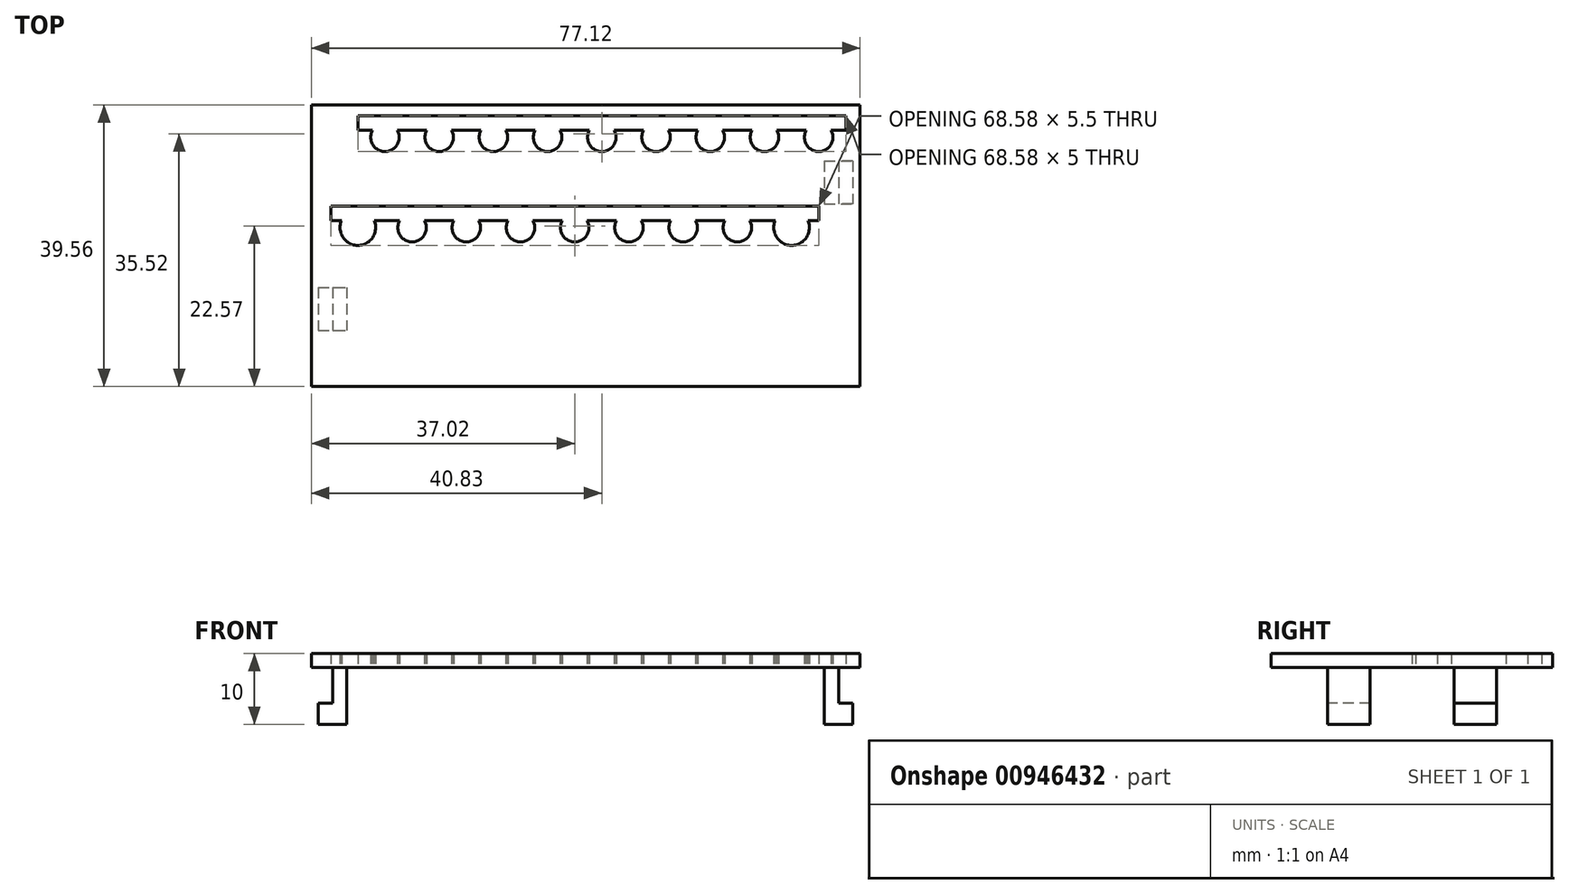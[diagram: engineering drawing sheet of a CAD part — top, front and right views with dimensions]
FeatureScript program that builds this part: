
annotation { "Feature Type Name" : "Feature", "Feature Type Description" : "" }
export const myFeature = defineFeature(function(context is Context, id is Id, definition is map)
    precondition{}
    {
        {
            var Q0;
            Q0=qCreatedBy(makeId("Top.planeOp"),FACE);
            var sketch = newSketch(context, id + "F0", { "sketchPlane" : qUnion([Q0])});
            skLineSegment(sketch, "E0.bottom", {"start": v(0, 39.56) * mm, "end": v(77.12, 39.56) * mm});
            skLineSegment(sketch, "E0.top", {"start": v(0, 0) * mm, "end": v(77.12, 0) * mm});
            skLineSegment(sketch, "E0.left", {"start": v(0, 39.56) * mm, "end": v(0, 0) * mm});
            skLineSegment(sketch, "E0.right", {"start": v(77.12, 39.56) * mm, "end": v(77.12, 0) * mm});
            skCircle(sketch, "E1", {"center": v(10.35, 35.02) * mm, "radius": 2 * mm});
            skCircle(sketch, "E2", {"center": v(14.16, 22.32) * mm, "radius": 2 * mm});
            skCircle(sketch, "E3.1.0.0", {"center": v(17.97, 35.02) * mm, "radius": 2 * mm});
            skCircle(sketch, "E3.2.0.0", {"center": v(25.6, 35.02) * mm, "radius": 2 * mm});
            skCircle(sketch, "E3.3.0.0", {"center": v(33.2, 35.02) * mm, "radius": 2 * mm});
            skCircle(sketch, "E3.4.0.0", {"center": v(40.83, 35.02) * mm, "radius": 2 * mm});
            skCircle(sketch, "E3.5.0.0", {"center": v(48.45, 35.02) * mm, "radius": 2 * mm});
            skCircle(sketch, "E3.6.0.0", {"center": v(56.07, 35.02) * mm, "radius": 2 * mm});
            skCircle(sketch, "E3.7.0.0", {"center": v(63.7, 35.02) * mm, "radius": 2 * mm});
            skCircle(sketch, "E3.8.0.0", {"center": v(71.31, 35.02) * mm, "radius": 2 * mm});
            skLineSegment(sketch, "E3.direction1", {"start": v(10.35, 35.02) * mm, "end": v(17.97, 35.02) * mm, "construction": true});
            skCircle(sketch, "E4.1.0.0", {"center": v(21.78, 22.32) * mm, "radius": 2 * mm});
            skCircle(sketch, "E4.2.0.0", {"center": v(29.4, 22.32) * mm, "radius": 2 * mm});
            skCircle(sketch, "E4.3.0.0", {"center": v(37.02, 22.32) * mm, "radius": 2 * mm});
            skCircle(sketch, "E4.4.0.0", {"center": v(44.64, 22.32) * mm, "radius": 2 * mm});
            skCircle(sketch, "E4.5.0.0", {"center": v(52.26, 22.32) * mm, "radius": 2 * mm});
            skCircle(sketch, "E4.6.0.0", {"center": v(59.88, 22.32) * mm, "radius": 2 * mm});
            skLineSegment(sketch, "E4.direction1", {"start": v(14.16, 22.32) * mm, "end": v(21.78, 22.32) * mm, "construction": true});
            skCircle(sketch, "E5", {"center": v(6.54, 22.32) * mm, "radius": 2.5 * mm});
            skCircle(sketch, "E6.1.0.0", {"center": v(67.5, 22.32) * mm, "radius": 2.5 * mm});
            skLineSegment(sketch, "E6.direction1", {"start": v(6.54, 22.32) * mm, "end": v(67.5, 22.32) * mm, "construction": true});
            skLineSegment(sketch, "E7.bottom", {"start": v(72.12, 31.67) * mm, "end": v(74.12, 31.67) * mm});
            skLineSegment(sketch, "E7.top", {"start": v(72.12, 25.67) * mm, "end": v(74.12, 25.67) * mm});
            skLineSegment(sketch, "E7.left", {"start": v(72.12, 31.67) * mm, "end": v(72.12, 25.67) * mm});
            skLineSegment(sketch, "E7.right", {"start": v(74.12, 31.67) * mm, "end": v(74.12, 25.67) * mm});
            skLineSegment(sketch, "E8.bottom", {"start": v(3, 13.89) * mm, "end": v(5, 13.89) * mm});
            skLineSegment(sketch, "E8.top", {"start": v(3, 7.89) * mm, "end": v(5, 7.89) * mm});
            skLineSegment(sketch, "E8.left", {"start": v(3, 13.89) * mm, "end": v(3, 7.89) * mm});
            skLineSegment(sketch, "E8.right", {"start": v(5, 13.89) * mm, "end": v(5, 7.89) * mm});
            skLineSegment(sketch, "E9.bottom", {"start": v(2.73, 25.32) * mm, "end": v(71.31, 25.32) * mm});
            skLineSegment(sketch, "E9.top", {"start": v(2.73, 23.32) * mm, "end": v(71.31, 23.32) * mm});
            skLineSegment(sketch, "E9.left", {"start": v(2.73, 25.32) * mm, "end": v(2.73, 23.32) * mm});
            skLineSegment(sketch, "E9.right", {"start": v(71.31, 25.32) * mm, "end": v(71.31, 23.32) * mm});
            skLineSegment(sketch, "E10.bottom", {"start": v(6.54, 38.02) * mm, "end": v(75.12, 38.02) * mm});
            skLineSegment(sketch, "E10.top", {"start": v(6.54, 36.02) * mm, "end": v(75.12, 36.02) * mm});
            skLineSegment(sketch, "E10.left", {"start": v(6.54, 38.02) * mm, "end": v(6.54, 36.02) * mm});
            skLineSegment(sketch, "E10.right", {"start": v(75.12, 38.02) * mm, "end": v(75.12, 36.02) * mm});
            skSolve(sketch);
        }
        {
            var Q0;
            Q0=makeQuery(id+"F0.imprint","IMPRINT",FACE,{"disambiguationData":[TD([[makeQuery(id+"F0.imprint","IMPRINT",EDGE,{"derivedFrom":sQuery(id+"F0.wireOp",EDGE,"E0.bottom")}),-1.0]])]});
            extrude(context, id + "F1", {"entities" : qUnion([Q0]), "depth" : 2 * mm, "offsetDistance" : 25 * mm});
        }
        {
            var Q0;
            Q0=makeQuery(id+"F0.imprint","IMPRINT",FACE,{"disambiguationData":[TD([[makeQuery(id+"F0.imprint","IMPRINT",EDGE,{"derivedFrom":sQuery(id+"F0.wireOp",EDGE,"E7.bottom")}),-1.0]])]});
            extrude(context, id + "F2", {"entities" : qUnion([Q0]), "operationType" : NewBodyOperationType.ADD, "depth" : -8 * mm, "offsetDistance" : 25 * mm, "hasSecondDirection" : true, "secondDirectionOppositeDirection" : true, "secondDirectionDepth" : -2 * mm});
        }
        {
            var Q0;
            Q0=makeQuery(id+"F0.imprint","IMPRINT",FACE,{"disambiguationData":[TD([[makeQuery(id+"F0.imprint","IMPRINT",EDGE,{"derivedFrom":sQuery(id+"F0.wireOp",EDGE,"E8.bottom")}),-1.0]])]});
            extrude(context, id + "F3", {"entities" : qUnion([Q0]), "operationType" : NewBodyOperationType.ADD, "depth" : -8 * mm, "offsetDistance" : 25 * mm, "hasSecondDirection" : true, "secondDirectionOppositeDirection" : true, "secondDirectionDepth" : -2 * mm});
        }
        {
            var Q0;
            Q0=makeQuery(id+"F3.opExtrude","SWEPT_FACE",FACE,{"disambiguationData":[OSD([sQuery(id+"F0.wireOp",EDGE,"E8.right")])]});
            var sketch = newSketch(context, id + "F4", { "sketchPlane" : qUnion([Q0])});
            skLineSegment(sketch, "E11.bottom", {"start": v(7.89, -5) * mm, "end": v(13.89, -5) * mm});
            skLineSegment(sketch, "E11.top", {"start": v(7.89, -8) * mm, "end": v(13.89, -8) * mm});
            skLineSegment(sketch, "E11.left", {"start": v(7.89, -5) * mm, "end": v(7.89, -8) * mm});
            skLineSegment(sketch, "E11.right", {"start": v(13.89, -5) * mm, "end": v(13.89, -8) * mm});
            skSolve(sketch);
        }
        {
            var Q0;
            Q0=makeQuery(id+"F4.imprint","IMPRINT",FACE,{"disambiguationData":[TD([[makeQuery(id+"F4.imprint","IMPRINT",EDGE,{"derivedFrom":sQuery(id+"F4.wireOp",EDGE,"E11.bottom")}),-1.0]])]});
            extrude(context, id + "F5", {"entities" : qUnion([Q0]), "operationType" : NewBodyOperationType.ADD, "depth" : -4 * mm, "offsetDistance" : 25 * mm});
        }
        {
            var Q0;
            Q0=makeQuery(id+"F2.opExtrude","SWEPT_FACE",FACE,{"disambiguationData":[OSD([sQuery(id+"F0.wireOp",EDGE,"E7.left")])]});
            var sketch = newSketch(context, id + "F6", { "sketchPlane" : qUnion([Q0])});
            skLineSegment(sketch, "E12.bottom", {"start": v(-31.67, -5) * mm, "end": v(-25.67, -5) * mm});
            skLineSegment(sketch, "E12.top", {"start": v(-31.67, -8) * mm, "end": v(-25.67, -8) * mm});
            skLineSegment(sketch, "E12.left", {"start": v(-31.67, -5) * mm, "end": v(-31.67, -8) * mm});
            skLineSegment(sketch, "E12.right", {"start": v(-25.67, -5) * mm, "end": v(-25.67, -8) * mm});
            skSolve(sketch);
        }
        {
            var Q0;
            Q0=makeQuery(id+"F6.imprint","IMPRINT",FACE,{"disambiguationData":[TD([[makeQuery(id+"F6.imprint","IMPRINT",EDGE,{"derivedFrom":sQuery(id+"F6.wireOp",EDGE,"E12.bottom")}),-1.0]])]});
            extrude(context, id + "F7", {"entities" : qUnion([Q0]), "operationType" : NewBodyOperationType.ADD, "depth" : -4 * mm, "offsetDistance" : 25 * mm});
        }
    });
